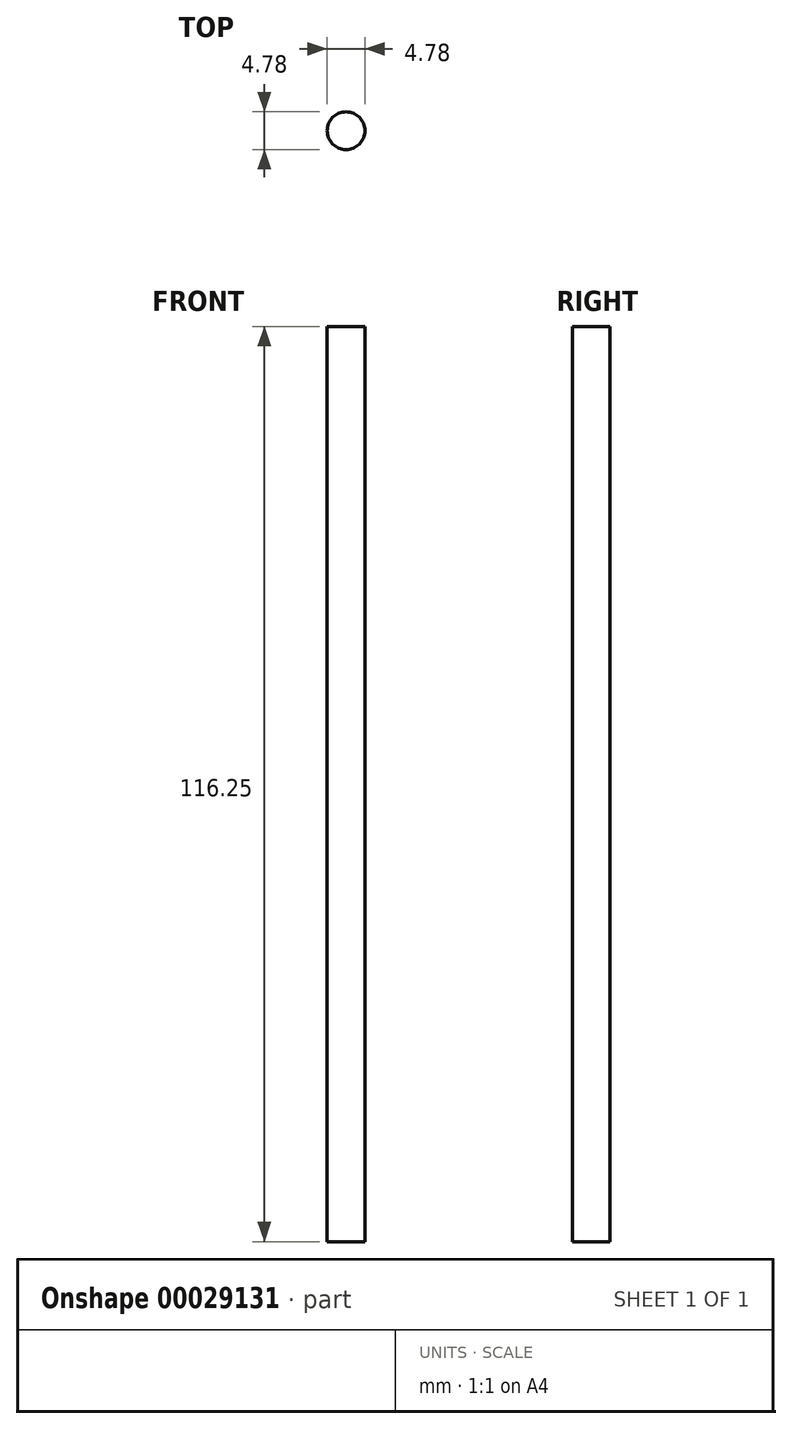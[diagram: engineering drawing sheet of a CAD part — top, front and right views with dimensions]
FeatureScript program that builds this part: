
annotation { "Feature Type Name" : "Feature", "Feature Type Description" : "" }
export const myFeature = defineFeature(function(context is Context, id is Id, definition is map)
    precondition{}
    {
        {
            var Q0;
            Q0=qCreatedBy(makeId("Top.planeOp"),FACE);
            var sketch = newSketch(context, id + "F0", { "sketchPlane" : qUnion([Q0])});
            skCircle(sketch, "E0", {"center": v(33.32, -8.88) * mm, "radius": 2.4 * mm});
            skSolve(sketch);
        }
        {
            var Q0;
            Q0=qSketchRegion(id+"F0",true);
            extrude(context, id + "F1", {"entities" : qUnion([Q0]), "oppositeDirection" : true, "depth" : 116.25 * mm});
        }
    });
